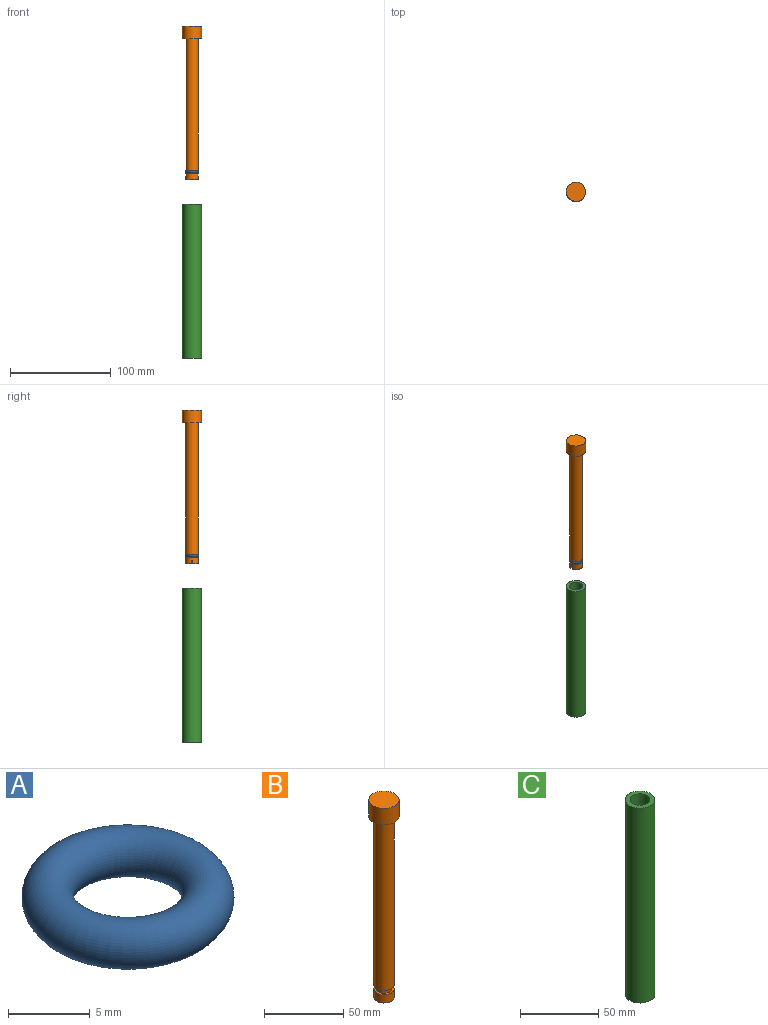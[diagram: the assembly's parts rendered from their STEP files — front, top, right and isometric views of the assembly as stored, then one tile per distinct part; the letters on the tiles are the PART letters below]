
ASSEMBLY  parts=3 mates=2
PART A: 1 faces, bbox 14x14x3.2 mm
  f0: torus R=4.9mm, axis (0,0,-1), area 307.2mm2
PART B: 17 faces, bbox 19.1x19.1x152.4 mm
  f0: plane 12.6x5.56mm, normal (0,0,-1), area 25.2mm2, adj f1,f11,f12,f16
  f1: cylinder r=6.35mm len=12.7mm, axis (0,0,-1), area 243.2mm2, adj f0,f8,f9,f10,f11,f12,f13,f14
  f2: cylinder r=6.35mm len=130.18mm, axis (0,0,-1), area 5193.8mm2, adj f4,f7
  f3: cylinder r=9.53mm len=19.05mm, axis (0,0,1), area 760.1mm2, adj f4,f5
  f4: plane 19.05x19.05mm, normal (0,0,-1), area 158.3mm2, adj f2,f3
  f5: plane 19.05x19.05mm, normal (0,0,1), area 285mm2, adj f3
  f6: cylinder r=4.76mm len=9.53mm, axis (0,0,-1), area 95mm2, adj f7,f8
  f7: plane 12.7x12.7mm, normal (0,0,-1), area 55.4mm2, adj f2,f6
  f8: plane 12.7x12.7mm, normal (0,0,1), area 55.4mm2, adj f1,f6
  f9: plane 12.6x5.56mm, normal (0,0,-1), area 25.2mm2, adj f1,f10,f13,f15
  f10: plane 3.18x1.6mm, normal (0,1,0), area 5.1mm2, adj f1,f9,f14,f15
  f11: plane 3.18x1.6mm, normal (0,-1,0), area 5.1mm2, adj f0,f1,f14,f16
  f12: plane 3.18x1.6mm, normal (0,-1,0), area 5.1mm2, adj f0,f1,f14,f16
  f13: plane 3.18x1.6mm, normal (0,1,0), area 5.1mm2, adj f1,f9,f14,f15
  f14: plane 12.7x9.53mm, normal (0,0,-1), area 76.3mm2, adj f1,f10,f11,f12,f13,f15,f16
  f15: cylinder r=4.76mm len=9.39mm, axis (0,0,-1), area 42.4mm2, adj f9,f10,f13,f14
  f16: cylinder r=4.76mm len=9.39mm, axis (0,0,-1), area 42.4mm2, adj f0,f11,f12,f14
PART C: 5 faces, bbox 19.1x19.1x152.4 mm
  f0: cylinder r=9.53mm len=152.4mm, axis (0,0,-1), area 9120.7mm2, adj f1,f2
  f1: plane 19.05x19.05mm, normal (0,0,1), area 158.3mm2, adj f0,f3
  f2: plane 19.05x19.05mm, normal (0,0,-1), area 285mm2, adj f0
  f3: cylinder r=6.35mm len=139.7mm, axis (0,0,-1), area 5573.8mm2, adj f1,f4
  f4: plane 12.7x12.7mm, normal (0,0,1), area 126.7mm2, adj f3
PLACE A t=(-59.35,22.85,206.76)mm
PLACE B t=(-59.06,22.85,275.02)mm
PLACE C t=(-59.06,22.85,98.18)mm
MATE pin_slot A.f0 <-> B.f3  axis (0,0,-1) through (-59.35,22.85,206.76)mm
MATE slider C.f0 <-> B.f3  axis (0,0,1) through (-59.06,22.85,174.38)mm
